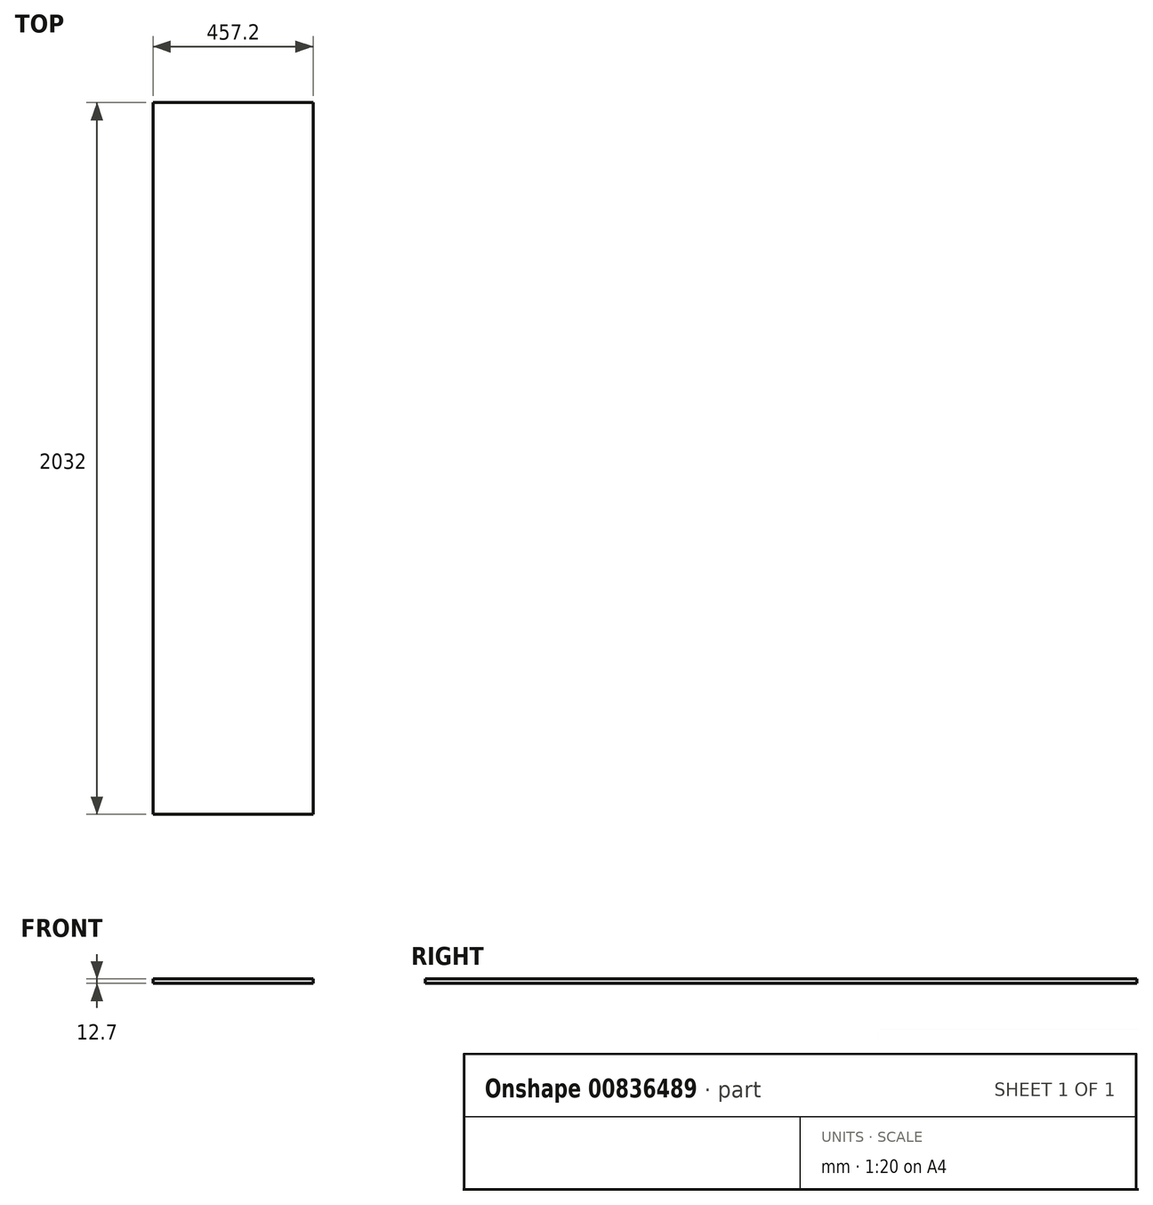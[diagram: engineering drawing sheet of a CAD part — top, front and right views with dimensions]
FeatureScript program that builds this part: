
annotation { "Feature Type Name" : "Feature", "Feature Type Description" : "" }
export const myFeature = defineFeature(function(context is Context, id is Id, definition is map)
    precondition{}
    {
        {
            var Q0;
            Q0=qCreatedBy(makeId("Top.planeOp"),FACE);
            var sketch = newSketch(context, id + "F0", { "sketchPlane" : qUnion([Q0])});
            skLineSegment(sketch, "E0.bottom", {"start": v(0, 0) * mm, "end": v(-457.2, 0) * mm});
            skLineSegment(sketch, "E0.top", {"start": v(0, 2032) * mm, "end": v(-457.2, 2032) * mm});
            skLineSegment(sketch, "E0.left", {"start": v(0, 0) * mm, "end": v(0, 2032) * mm});
            skLineSegment(sketch, "E0.right", {"start": v(-457.2, 0) * mm, "end": v(-457.2, 2032) * mm});
            skSolve(sketch);
        }
        {
            var Q0;
            Q0=makeQuery(id+"F0.imprint","IMPRINT",FACE,{"disambiguationData":[TD([[makeQuery(id+"F0.imprint","IMPRINT",EDGE,{"derivedFrom":sQuery(id+"F0.wireOp",EDGE,"E0.bottom")}),-1.0]])]});
            extrude(context, id + "F1", {"entities" : qUnion([Q0]), "depth" : 12.7 * mm, "offsetDistance" : 25.4 * mm});
        }
    });
